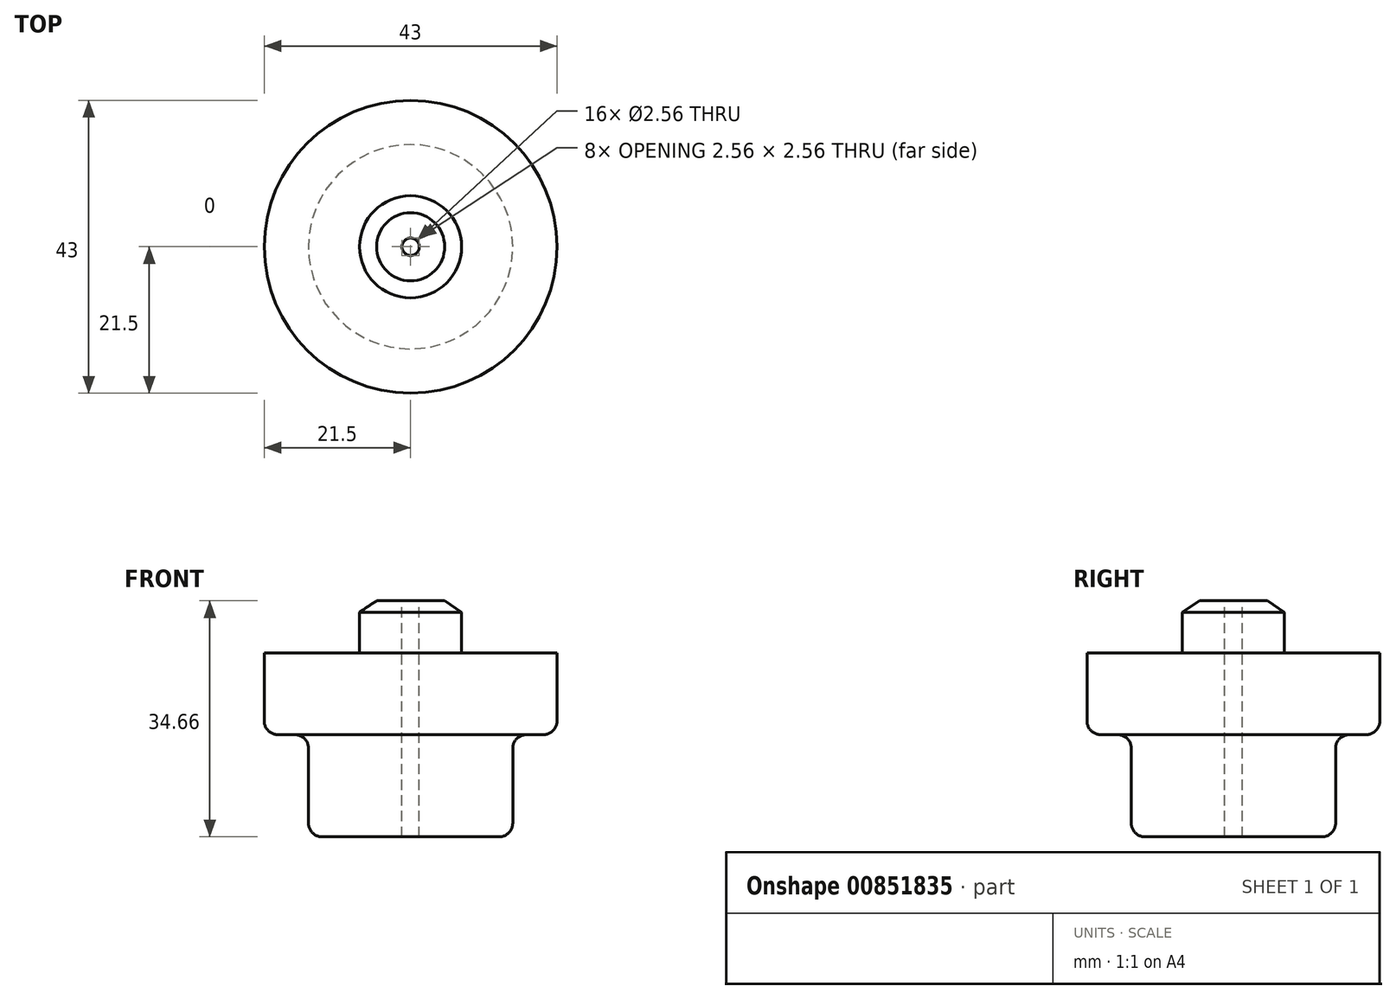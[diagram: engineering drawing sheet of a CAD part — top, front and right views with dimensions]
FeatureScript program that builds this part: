
annotation { "Feature Type Name" : "Feature", "Feature Type Description" : "" }
export const myFeature = defineFeature(function(context is Context, id is Id, definition is map)
    precondition{}
    {
        {
            var Q0;
            Q0=qCreatedBy(makeId("Front.planeOp"),FACE);
            var sketch = newSketch(context, id + "F0", { "sketchPlane" : qUnion([Q0])});
            skLineSegment(sketch, "E0", {"start": v(0, 0) * mm, "end": v(0, 51.73) * mm, "construction": true});
            skLineSegment(sketch, "E1", {"start": v(0, 0) * mm, "end": v(-15, 0) * mm});
            skLineSegment(sketch, "E2", {"start": v(-15, 0) * mm, "end": v(-15, 15) * mm});
            skLineSegment(sketch, "E3", {"start": v(-15, 15) * mm, "end": v(-21.5, 15) * mm});
            skLineSegment(sketch, "E4", {"start": v(-21.5, 15) * mm, "end": v(-21.5, 27) * mm});
            skLineSegment(sketch, "E5", {"start": v(-21.5, 27) * mm, "end": v(-7.5, 27) * mm});
            skLineSegment(sketch, "E6", {"start": v(-7.5, 27) * mm, "end": v(-7.5, 33) * mm});
            skLineSegment(sketch, "E7", {"start": v(-7.5, 33) * mm, "end": v(-5, 34.66) * mm});
            skLineSegment(sketch, "E8", {"start": v(-5, 34.66) * mm, "end": v(0, 34.66) * mm});
            skLineSegment(sketch, "E9", {"start": v(-15, 0) * mm, "end": v(0, 0) * mm});
            skLineSegment(sketch, "E10", {"start": v(0, 34.66) * mm, "end": v(0, 0) * mm});
            skSolve(sketch);
        }
        {
            var Q0;
            Q0=makeQuery(id+"F0.imprint","IMPRINT",FACE,{"disambiguationData":[TD([[makeQuery(id+"F0.imprint","IMPRINT",EDGE,{"derivedFrom":sQuery(id+"F0.wireOp",EDGE,"E2")}),-1.0]])]});
            var Q1;
            Q1=sQuery(id+"F0.wireOp",EDGE,"E0");
            revolve(context, id + "F1", {"surfaceOperationType" : NewSurfaceOperationType.NEW, "entities" : qUnion([Q0]), "axis" : qUnion([Q1]), "revolveType" : RevolveType.FULL});
        }
        {
            var Q0;
            Q0=makeQuery(id+"F1.opRevolve","SWEPT_FACE",FACE,{"disambiguationData":[OSD([sQuery(id+"F0.wireOp",EDGE,"E8")])]});
            var sketch = newSketch(context, id + "F2", { "sketchPlane" : qUnion([Q0])});
            skCircle(sketch, "E11", {"center": v(0, 0) * mm, "radius": 1.28 * mm});
            skSolve(sketch);
        }
        {
            var Q0;
            Q0=makeQuery(id+"F2.imprint","IMPRINT",FACE,{"disambiguationData":[TD([[makeQuery(id+"F2.imprint","IMPRINT",EDGE,{"derivedFrom":sQuery(id+"F2.wireOp",EDGE,"E11")}),1.0]])]});
            extrude(context, id + "F3", {"entities" : qUnion([Q0]), "operationType" : NewBodyOperationType.REMOVE, "endBound" : BoundingType.THROUGH_ALL, "oppositeDirection" : true, "depth" : 22 * mm, "offsetDistance" : 25 * mm});
        }
        {
            var Q0;
            Q0=makeQuery(id+"F1.opRevolve","SWEPT_EDGE",EDGE,{"disambiguationData":[OSD([sQuery(id+"F0.wireOp",EDGE,"E3"),sQuery(id+"F0.wireOp",EDGE,"E4")])]});
            fillet(context, id + "F4", {"entities" : qUnion([Q0]), "radius" : 2 * mm, "tangentPropagation" : true, "allowEdgeOverflow" : false});
        }
        {
            var Q0;
            Q0=makeQuery(id+"F1.opRevolve","SWEPT_EDGE",EDGE,{"disambiguationData":[OSD([sQuery(id+"F0.wireOp",EDGE,"E2"),sQuery(id+"F0.wireOp",EDGE,"E9")])]});
            fillet(context, id + "F5", {"entities" : qUnion([Q0]), "radius" : 2 * mm, "tangentPropagation" : true, "allowEdgeOverflow" : false});
        }
    });
